# Revit family: Toilet-Wall_Mount-KOHLER-VEIL-K-5402SA_1
name_source: partatom
category: Plumbing Fixtures
revit_build: Autodesk Revit 2017 (Build: 20160225_1515(x64)
units: mm (PartAtom-declared; Revit-internal decimal feet)

## family parameters
Cut with Voids When Loaded = No
Host = Face
OmniClass Number = 23.31.19.00
OmniClass Title = Toilets
Part Type = Normal
Room Calculation Point = No
Round Connector Dimension = Use Diameter
Shared = No

## types (1)
- 0-White
    ADA Compliant = No
    Apparent Load = 2200 VA
    Assembly Code = D2010100
    CW Connection = Yes
    Cold Water Inlet = Cold Water Inlet
    Date Modified = 01/13/2021
    Default Elevation = 0"
    Description = Wall Hung Intelligent Toilet
    Electrical Connector = Yes
    Electrical Note = Connect to a properly grounded, grounding -type receptacle which is protected by a Ground-Fault Circuit-Interrupter (GFCI) or Residual Current Device(RCD)
    Finish = Kohler-Vitreous_China-0-White
    Flow Rate = 0 GPM
    Flush Rate- GPF = 1.18 GPF
    Flush Rate- LPF = 4.42 LPF
    HW Connection = No
    Hot Water Inlet = Hot Water Inlet
    Length = 26 9/16"
    Manufacturer = KOHLER Co.
    Master Format 2014 = 22 41 13.13
    Master Format 2014 Name = Residential Water Closets
    Material = Vitreous China
    Model = K-5402SA-0
    Pressure = 107.00 psi
    Product Name = VEIL
    Rough-In = 6 1/8"
    Seat Included = Yes
    Type = 1
    URL = https://me.kohler.com
    Vent Connection = No
    Voltage = 220 V
    Waste Connection = Yes
    Waste Water Outlet = Waste Water Outlet
    WaterSense Certified = No
    Width = 17 1/4"

## geometry (parser evidence)
native form markers: Sweep x4
no freeform markers — native parametric forms only
